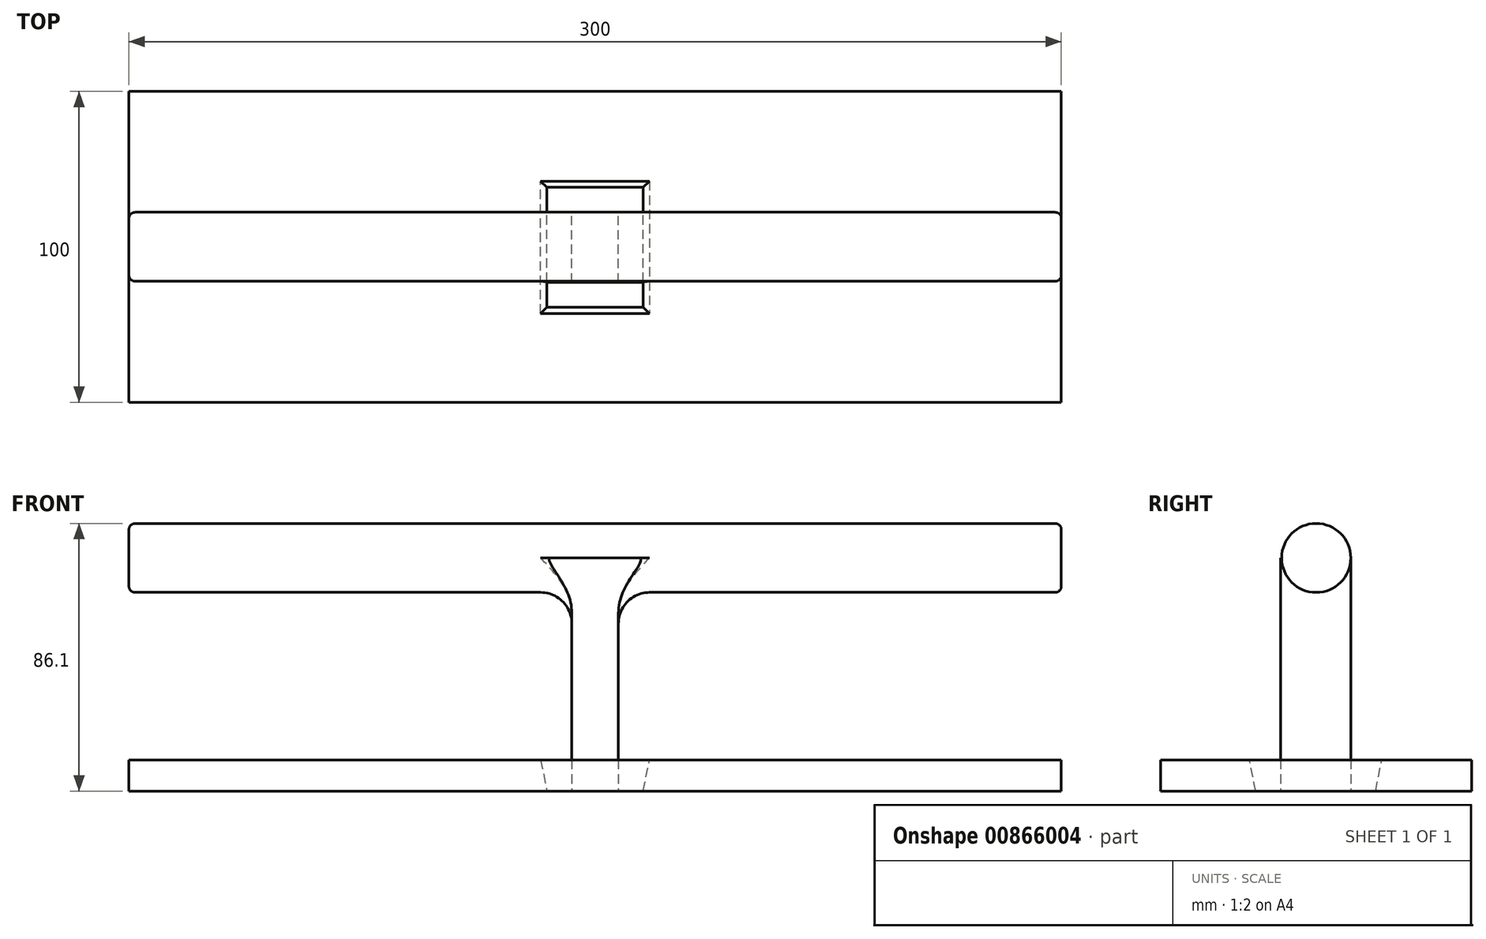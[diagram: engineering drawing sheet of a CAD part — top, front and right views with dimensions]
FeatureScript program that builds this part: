
annotation { "Feature Type Name" : "Feature", "Feature Type Description" : "" }
export const myFeature = defineFeature(function(context is Context, id is Id, definition is map)
    precondition{}
    {
        {
            var Q0;
            Q0=qCreatedBy(makeId("Right.planeOp"),FACE);
            var sketch = newSketch(context, id + "F0", { "sketchPlane" : qUnion([Q0])});
            skCircle(sketch, "E0", {"center": v(0, 0) * mm, "radius": 11.1 * mm});
            skSolve(sketch);
        }
        {
            var Q0;
            Q0=makeQuery(id+"F0.imprint","IMPRINT",FACE,{"disambiguationData":[TD([[makeQuery(id+"F0.imprint","IMPRINT",EDGE,{"derivedFrom":sQuery(id+"F0.wireOp",EDGE,"E0")}),1.0]])]});
            extrude(context, id + "F1", {"entities" : qUnion([Q0]), "endBound" : BoundingType.SYMMETRIC, "depth" : 300 * mm});
        }
        {
            var Q0;
            Q0=qCreatedBy(makeId("Right.planeOp"),FACE);
            var sketch = newSketch(context, id + "F2", { "sketchPlane" : qUnion([Q0])});
            skLineSegment(sketch, "E1.bottom", {"start": v(-11.46, 0) * mm, "end": v(11.1, 0) * mm});
            skLineSegment(sketch, "E1.top", {"start": v(-11.46, -75) * mm, "end": v(11.1, -75) * mm});
            skLineSegment(sketch, "E1.left", {"start": v(-11.46, 0) * mm, "end": v(-11.46, -75) * mm});
            skLineSegment(sketch, "E1.right", {"start": v(11.1, 0) * mm, "end": v(11.1, -75) * mm});
            skSolve(sketch);
        }
        {
            var Q0;
            Q0=makeQuery(id+"F2.imprint","IMPRINT",FACE,{"disambiguationData":[TD([[makeQuery(id+"F2.imprint","IMPRINT",EDGE,{"derivedFrom":sQuery(id+"F2.wireOp",EDGE,"E1.bottom")}),-1.0]])]});
            var sketch = newSketch(context, id + "F3", { "sketchPlane" : qUnion([Q0])});
            skSolve(sketch);
        }
        {
            var Q0;
            Q0=qSketchRegion(id+"F3",true);
            var Q1;
            Q1=makeQuery(id+"F2.imprint","IMPRINT",FACE,{"disambiguationData":[TD([[makeQuery(id+"F2.imprint","IMPRINT",EDGE,{"derivedFrom":sQuery(id+"F2.wireOp",EDGE,"E1.bottom")}),-1.0]])]});
            extrude(context, id + "F4", {"entities" : qUnion([Q0, Q1]), "operationType" : NewBodyOperationType.ADD, "endBound" : BoundingType.SYMMETRIC, "depth" : 15 * mm});
        }
        {
            var Q0;
            Q0=makeQuery(id+"F4.opExtrude","SWEPT_FACE",FACE,{"disambiguationData":[OSD([sQuery(id+"F2.wireOp",EDGE,"E1.top")])]});
            var sketch = newSketch(context, id + "F5", { "sketchPlane" : qUnion([Q0])});
            skLineSegment(sketch, "E2.bottom", {"start": v(150, 50) * mm, "end": v(-150, 50) * mm});
            skLineSegment(sketch, "E2.top", {"start": v(150, -50) * mm, "end": v(-150, -50) * mm});
            skLineSegment(sketch, "E2.left", {"start": v(150, 50) * mm, "end": v(150, -50) * mm});
            skLineSegment(sketch, "E2.right", {"start": v(-150, 50) * mm, "end": v(-150, -50) * mm});
            skPoint(sketch, "E2.middle", {"position": v(0, 0) * mm});
            skSolve(sketch);
        }
        {
            var Q0;
            Q0=makeQuery(id+"F1.opExtrude","CAP_EDGE",EDGE,{"disambiguationData":[OSD([sQuery(id+"F0.wireOp",EDGE,"E0")])],"isStart":true});
            var Q1;
            Q1=makeQuery(id+"F1.opExtrude","CAP_EDGE",EDGE,{"disambiguationData":[OSD([sQuery(id+"F0.wireOp",EDGE,"E0")])],"isStart":false});
            fillet(context, id + "F6", {"entities" : qUnion([Q0, Q1]), "radius" : 2 * mm, "tangentPropagation" : true, "allowEdgeOverflow" : false});
        }
        {
            var Q0;
            Q0=makeQuery(id+"F5.imprint","IMPRINT",FACE,{"disambiguationData":[TD([[makeQuery(id+"F5.imprint","IMPRINT",EDGE,{"derivedFrom":sQuery(id+"F5.wireOp",EDGE,"E2.bottom")}),1.0]])]});
            extrude(context, id + "F7", {"entities" : qUnion([Q0]), "oppositeDirection" : true, "depth" : 10 * mm});
        }
        {
            var Q0;
            {var subQ0=sQuery(id+"F2.wireOp",EDGE,"E1.top");Q0=makeQuery(id+"F7.opExtrude","CAP_EDGE",EDGE,{"disambiguationData":[OSD([subQ0]),TDD([makeQuery(id+"F5.imprint","IMPRINT",EDGE,{"derivedFrom":makeQuery(id+"F4.opExtrude","CAP_EDGE",EDGE,{"disambiguationData":[OSD([subQ0])],"isStart":false})})])],"isStart":false});}
            var Q1;
            Q1=makeQuery(id+"F7.opExtrude","CAP_EDGE",EDGE,{"disambiguationData":[OSD([sQuery(id+"F2.wireOp",EDGE,"E1.top"),sQuery(id+"F2.wireOp",EDGE,"E1.left")])],"isStart":false});
            var Q2;
            Q2=makeQuery(id+"F7.opExtrude","CAP_EDGE",EDGE,{"disambiguationData":[OSD([sQuery(id+"F2.wireOp",EDGE,"E1.top"),sQuery(id+"F2.wireOp",EDGE,"E1.right")])],"isStart":false});
            var Q3;
            {var subQ0=sQuery(id+"F2.wireOp",EDGE,"E1.top");Q3=makeQuery(id+"F7.opExtrude","CAP_EDGE",EDGE,{"disambiguationData":[OSD([subQ0]),TDD([makeQuery(id+"F5.imprint","IMPRINT",EDGE,{"derivedFrom":makeQuery(id+"F4.opExtrude","CAP_EDGE",EDGE,{"disambiguationData":[OSD([subQ0])],"isStart":true})})])],"isStart":false});}
            chamfer(context, id + "F8", {"entities" : qUnion([Q0, Q1, Q2, Q3]), "chamferType" : ChamferType.TWO_OFFSETS, "width1" : 50 * mm, "oppositeDirection" : false, "width2" : 10 * mm, "tangentPropagation" : true});
        }
        {
            var Q0;
            Q0=makeQuery(id+"F4.boolean.opBoolean","INTERSECT",EDGE,{"derivedFrom":[makeQuery(id+"F1.opExtrude","SWEPT_FACE",FACE,{"disambiguationData":[OSD([sQuery(id+"F0.wireOp",EDGE,"E0")])]}),makeQuery(id+"F4.opExtrude","CAP_FACE",FACE,{"disambiguationData":[OSD([sQuery(id+"F2.wireOp",EDGE,"E1.bottom"),sQuery(id+"F2.wireOp",EDGE,"E1.top"),sQuery(id+"F2.wireOp",EDGE,"E1.left"),sQuery(id+"F2.wireOp",EDGE,"E1.right")])],"isStart":false})]});
            var Q1;
            Q1=makeQuery(id+"F4.boolean.opBoolean","INTERSECT",EDGE,{"derivedFrom":[makeQuery(id+"F1.opExtrude","SWEPT_FACE",FACE,{"disambiguationData":[OSD([sQuery(id+"F0.wireOp",EDGE,"E0")])]}),makeQuery(id+"F4.opExtrude","CAP_FACE",FACE,{"disambiguationData":[OSD([sQuery(id+"F2.wireOp",EDGE,"E1.bottom"),sQuery(id+"F2.wireOp",EDGE,"E1.top"),sQuery(id+"F2.wireOp",EDGE,"E1.left"),sQuery(id+"F2.wireOp",EDGE,"E1.right")])],"isStart":true})]});
            fillet(context, id + "F9", {"entities" : qUnion([Q0, Q1]), "radius" : 10 * mm, "tangentPropagation" : true, "allowEdgeOverflow" : false});
        }
    });
